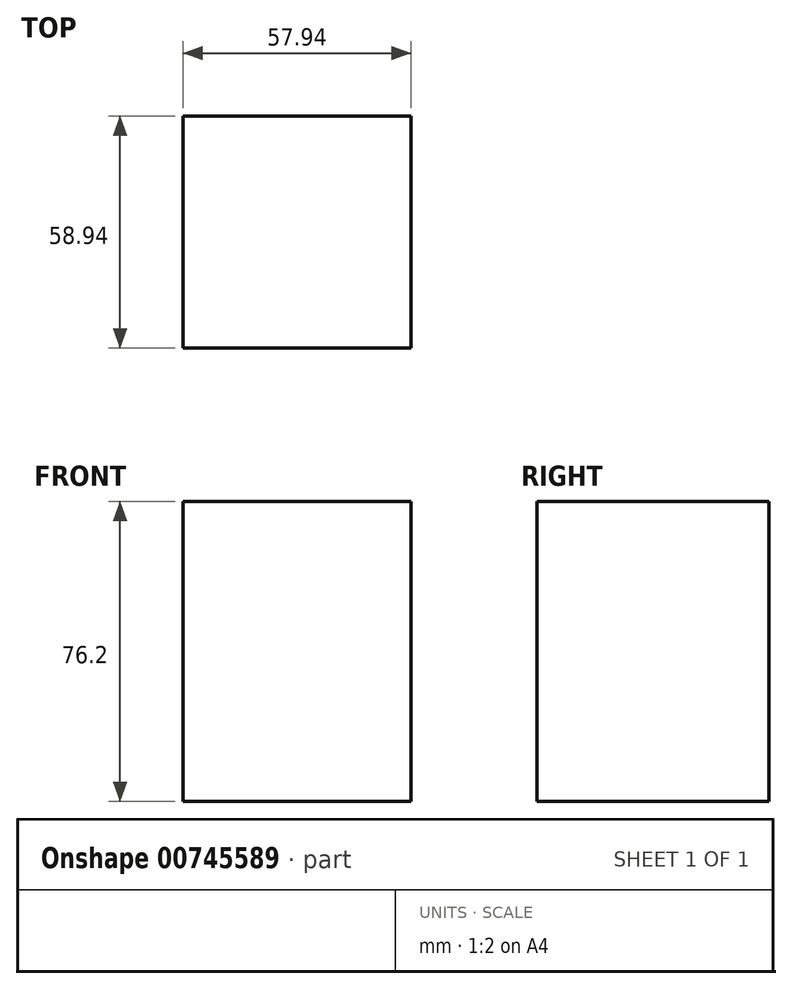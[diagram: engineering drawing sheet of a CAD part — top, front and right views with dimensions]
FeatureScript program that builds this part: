
annotation { "Feature Type Name" : "Feature", "Feature Type Description" : "" }
export const myFeature = defineFeature(function(context is Context, id is Id, definition is map)
    precondition{}
    {
        {
            var Q0;
            Q0=qCreatedBy(makeId("Top.planeOp"),FACE);
            var sketch = newSketch(context, id + "F0", { "sketchPlane" : qUnion([Q0])});
            skPoint(sketch, "E0.0", {"position": v(0, 0) * mm});
            skLineSegment(sketch, "E1.bottom", {"start": v(-28.97, 29.47) * mm, "end": v(28.97, 29.47) * mm});
            skLineSegment(sketch, "E1.top", {"start": v(-28.97, -29.47) * mm, "end": v(28.97, -29.47) * mm});
            skLineSegment(sketch, "E1.left", {"start": v(-28.97, 29.47) * mm, "end": v(-28.97, -29.47) * mm});
            skLineSegment(sketch, "E1.right", {"start": v(28.97, 29.47) * mm, "end": v(28.97, -29.47) * mm});
            skSolve(sketch);
        }
        {
            var Q0;
            Q0=makeQuery(id+"F0.imprint","IMPRINT",FACE,{"disambiguationData":[TD([[makeQuery(id+"F0.imprint","IMPRINT",EDGE,{"derivedFrom":sQuery(id+"F0.wireOp",EDGE,"E1.bottom")}),-1.0]])]});
            extrude(context, id + "F1", {"entities" : qUnion([Q0]), "depth" : 76.2 * mm, "offsetDistance" : 25.4 * mm});
        }
    });
